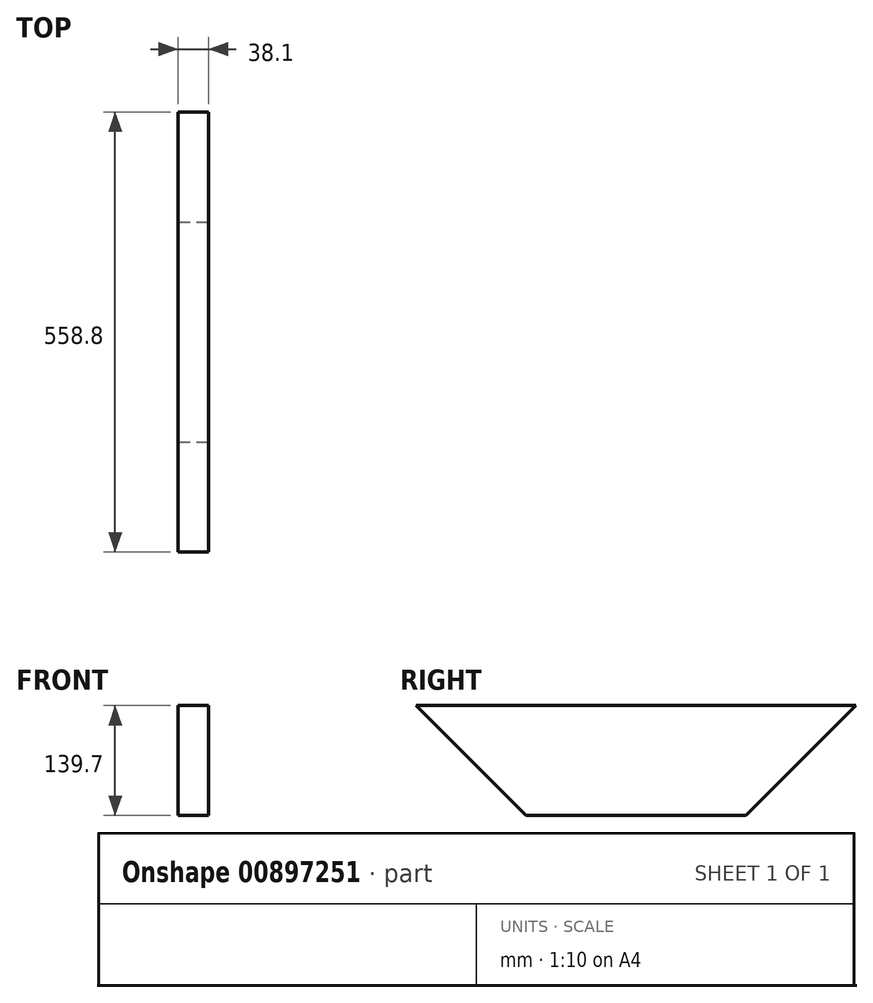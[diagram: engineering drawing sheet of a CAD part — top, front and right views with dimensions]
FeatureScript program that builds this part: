
annotation { "Feature Type Name" : "Feature", "Feature Type Description" : "" }
export const myFeature = defineFeature(function(context is Context, id is Id, definition is map)
    precondition{}
    {
        {
            var Q0;
            Q0=qCreatedBy(makeId("Front.planeOp"),FACE);
            var sketch = newSketch(context, id + "F0", { "sketchPlane" : qUnion([Q0])});
            skLineSegment(sketch, "E0.bottom", {"start": v(-19.05, 69.85) * mm, "end": v(19.05, 69.85) * mm});
            skLineSegment(sketch, "E0.top", {"start": v(-19.05, -69.85) * mm, "end": v(19.05, -69.85) * mm});
            skLineSegment(sketch, "E0.left", {"start": v(-19.05, 69.85) * mm, "end": v(-19.05, -69.85) * mm});
            skLineSegment(sketch, "E0.right", {"start": v(19.05, 69.85) * mm, "end": v(19.05, -69.85) * mm});
            skPoint(sketch, "E0.middle", {"position": v(0, 0) * mm});
            skSolve(sketch);
        }
        {
            var Q0;
            Q0=makeQuery(id+"F0.imprint","IMPRINT",FACE,{"disambiguationData":[TD([[makeQuery(id+"F0.imprint","IMPRINT",EDGE,{"derivedFrom":sQuery(id+"F0.wireOp",EDGE,"E0.bottom")}),-1.0]])]});
            extrude(context, id + "F1", {"entities" : qUnion([Q0]), "depth" : 279.4 * mm, "offsetDistance" : 25.4 * mm});
        }
        {
            var Q0;
            Q0=makeQuery(id+"F1.opExtrude","SWEPT_FACE",FACE,{"disambiguationData":[OSD([sQuery(id+"F0.wireOp",EDGE,"E0.right")])]});
            var sketch = newSketch(context, id + "F2", { "sketchPlane" : qUnion([Q0])});
            skLineSegment(sketch, "E1", {"start": v(-279.4, -69.85) * mm, "end": v(-419.1, 69.85) * mm});
            skLineSegment(sketch, "E2", {"start": v(0, -69.85) * mm, "end": v(139.7, 69.85) * mm});
            skLineSegment(sketch, "E3", {"start": v(-419.1, 69.85) * mm, "end": v(-279.4, 69.85) * mm});
            skLineSegment(sketch, "E4", {"start": v(-279.4, 69.85) * mm, "end": v(-279.4, -69.85) * mm});
            skLineSegment(sketch, "E5", {"start": v(139.7, 69.85) * mm, "end": v(0, 69.85) * mm});
            skLineSegment(sketch, "E6", {"start": v(0, 69.85) * mm, "end": v(0, -69.85) * mm});
            skSolve(sketch);
        }
        {
            var Q0;
            Q0 = qSketchRegion(id + "F2", true);
            var Q1;
            Q1=makeQuery(id+"F1.opExtrude","SWEPT_FACE",FACE,{"disambiguationData":[OSD([sQuery(id+"F0.wireOp",EDGE,"E0.left")])]});
            extrude(context, id + "F3", {"entities" : qUnion([Q0]), "operationType" : NewBodyOperationType.ADD, "endBound" : BoundingType.UP_TO_SURFACE, "oppositeDirection" : true, "depth" : 25.4 * mm, "endBoundEntityFace" : qUnion([Q1]), "offsetDistance" : 25.4 * mm});
        }
    });
